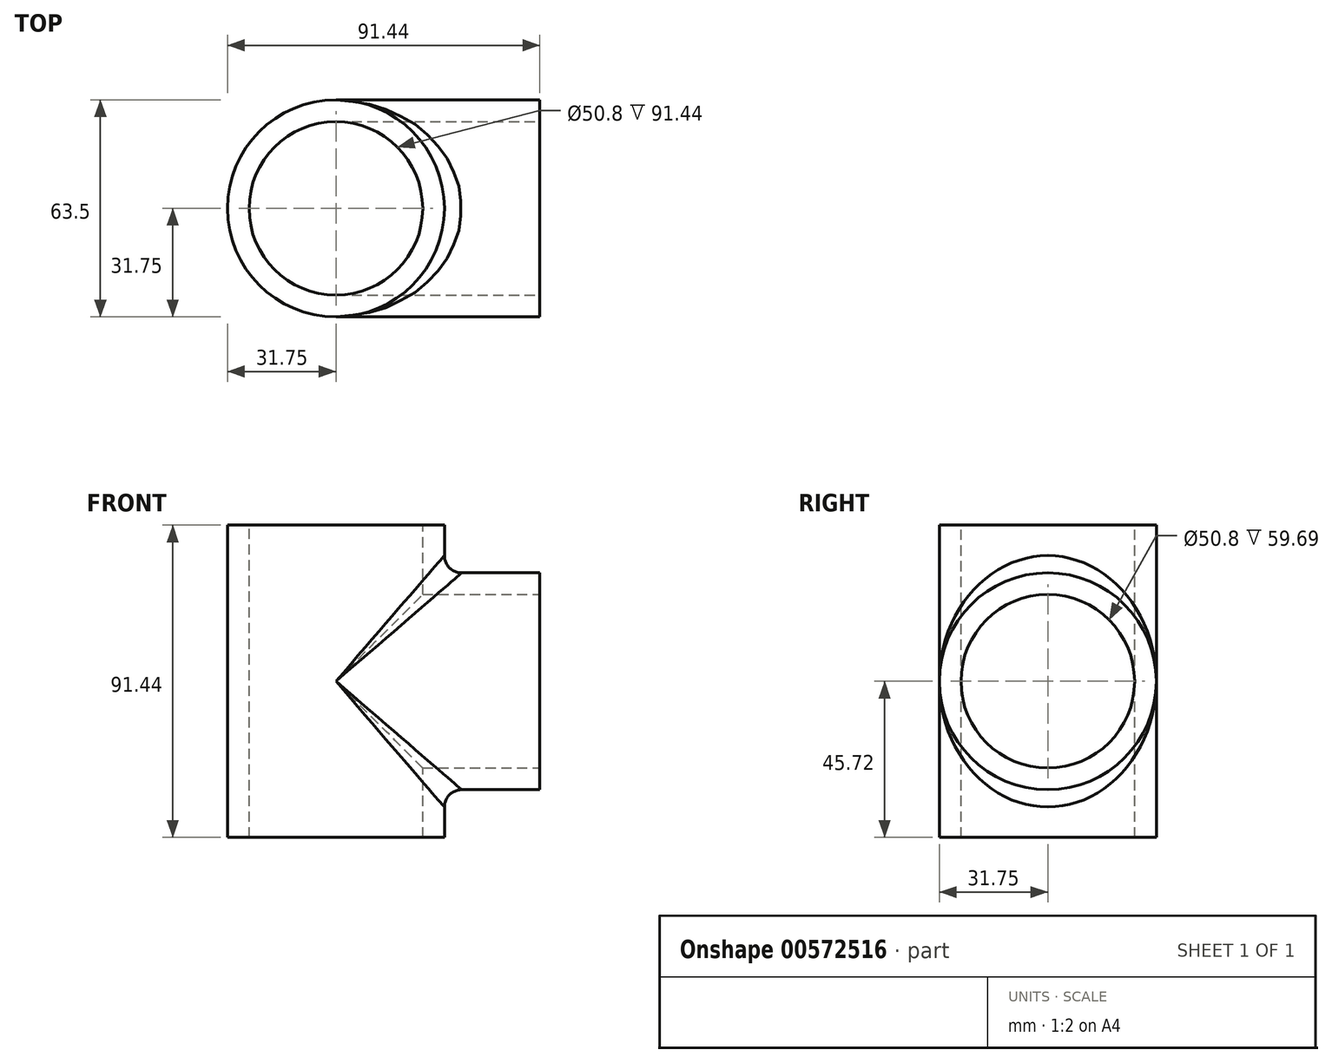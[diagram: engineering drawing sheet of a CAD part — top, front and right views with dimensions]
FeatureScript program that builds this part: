
annotation { "Feature Type Name" : "Feature", "Feature Type Description" : "" }
export const myFeature = defineFeature(function(context is Context, id is Id, definition is map)
    precondition{}
    {
        {
            var Q0;
            Q0=qCreatedBy(makeId("Top.planeOp"),FACE);
            var sketch = newSketch(context, id + "F0", { "sketchPlane" : qUnion([Q0])});
            skCircle(sketch, "E0", {"center": v(0, 0) * mm, "radius": 31.75 * mm});
            skSolve(sketch);
        }
        {
            var Q0;
            Q0 = qSketchRegion(id + "F0", true);
            extrude(context, id + "F1", {"entities" : qUnion([Q0]), "depth" : 45.72 * mm, "offsetDistance" : 25.4 * mm, "hasSecondDirection" : true, "secondDirectionOppositeDirection" : true, "secondDirectionDepth" : 45.72 * mm});
        }
        {
            var Q0;
            Q0=qCreatedBy(makeId("Right.planeOp"),FACE);
            var sketch = newSketch(context, id + "F2", { "sketchPlane" : qUnion([Q0])});
            skCircle(sketch, "E1", {"center": v(0, 0) * mm, "radius": 31.75 * mm});
            skSolve(sketch);
        }
        {
            var Q0;
            Q0 = qSketchRegion(id + "F2", true);
            extrude(context, id + "F3", {"entities" : qUnion([Q0]), "operationType" : NewBodyOperationType.ADD, "depth" : 59.69 * mm, "offsetDistance" : 25.4 * mm});
        }
        {
            var Q0;
            Q0=makeQuery(id+"F1.opExtrude","CAP_FACE",FACE,{"disambiguationData":[OSD([sQuery(id+"F0.wireOp",EDGE,"E0")])],"isStart":false});
            var sketch = newSketch(context, id + "F4", { "sketchPlane" : qUnion([Q0])});
            skCircle(sketch, "E2", {"center": v(0, 0) * mm, "radius": 25.4 * mm});
            skSolve(sketch);
        }
        {
            var Q0;
            Q0 = qSketchRegion(id + "F4", true);
            extrude(context, id + "F5", {"entities" : qUnion([Q0]), "operationType" : NewBodyOperationType.REMOVE, "endBound" : BoundingType.UP_TO_NEXT, "oppositeDirection" : true, "depth" : 25.4 * mm, "offsetDistance" : 25.4 * mm});
        }
        {
            var Q0;
            Q0=makeQuery(id+"F3.opExtrude","CAP_FACE",FACE,{"disambiguationData":[OSD([sQuery(id+"F2.wireOp",EDGE,"E1")])],"isStart":false});
            var sketch = newSketch(context, id + "F6", { "sketchPlane" : qUnion([Q0])});
            skCircle(sketch, "E3", {"center": v(0, 0) * mm, "radius": 25.4 * mm});
            skSolve(sketch);
        }
        {
            var Q0;
            Q0 = qSketchRegion(id + "F6", true);
            extrude(context, id + "F7", {"entities" : qUnion([Q0]), "operationType" : NewBodyOperationType.REMOVE, "endBound" : BoundingType.UP_TO_NEXT, "oppositeDirection" : true, "depth" : 25.4 * mm, "offsetDistance" : 25.4 * mm});
        }
        {
            var Q0;
            Q0=makeQuery(id+"F3.boolean.opBoolean","INTERSECT",EDGE,{"disambiguationData":[OD(1.0)],"derivedFrom":[makeQuery(id+"F1.opExtrude","SWEPT_FACE",FACE,{"disambiguationData":[OSD([sQuery(id+"F0.wireOp",EDGE,"E0")])]}),makeQuery(id+"F3.opExtrude","SWEPT_FACE",FACE,{"disambiguationData":[OSD([sQuery(id+"F2.wireOp",EDGE,"E1")])]})]});
            var Q1;
            Q1=makeQuery(id+"F3.boolean.opBoolean","INTERSECT",EDGE,{"disambiguationData":[OD(0.0)],"derivedFrom":[makeQuery(id+"F1.opExtrude","SWEPT_FACE",FACE,{"disambiguationData":[OSD([sQuery(id+"F0.wireOp",EDGE,"E0")])]}),makeQuery(id+"F3.opExtrude","SWEPT_FACE",FACE,{"disambiguationData":[OSD([sQuery(id+"F2.wireOp",EDGE,"E1")])]})]});
            fillet(context, id + "F8", {"entities" : qUnion([Q0, Q1]), "radius" : 5.08 * mm, "tangentPropagation" : true, "allowEdgeOverflow" : false});
        }
    });
